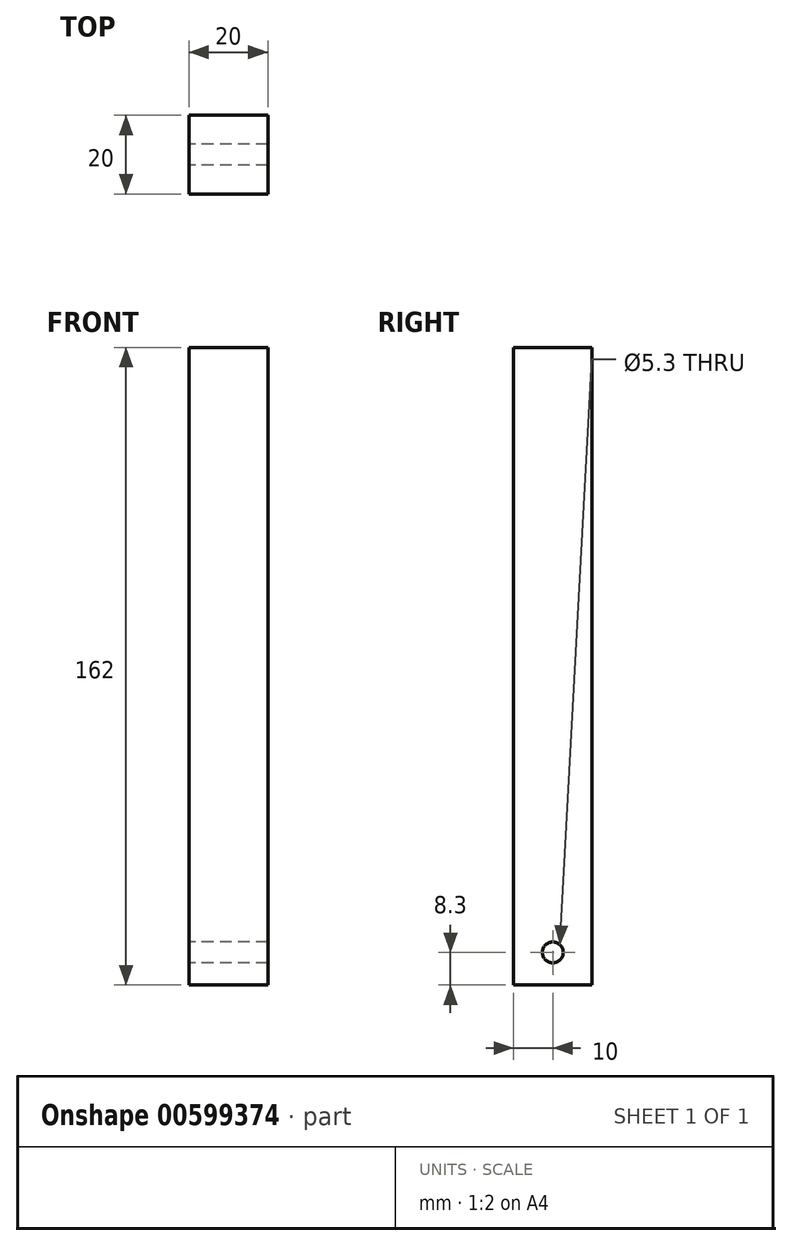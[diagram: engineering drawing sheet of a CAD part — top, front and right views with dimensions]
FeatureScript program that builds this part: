
annotation { "Feature Type Name" : "Feature", "Feature Type Description" : "" }
export const myFeature = defineFeature(function(context is Context, id is Id, definition is map)
    precondition{}
    {
        {
            var Q0;
            Q0=qCreatedBy(makeId("Top.planeOp"),FACE);
            var sketch = newSketch(context, id + "F0", { "sketchPlane" : qUnion([Q0])});
            skLineSegment(sketch, "E0.bottom", {"start": v(-10, 10) * mm, "end": v(10, 10) * mm});
            skLineSegment(sketch, "E0.top", {"start": v(-10, -10) * mm, "end": v(10, -10) * mm});
            skLineSegment(sketch, "E0.left", {"start": v(-10, 10) * mm, "end": v(-10, -10) * mm});
            skLineSegment(sketch, "E0.right", {"start": v(10, 10) * mm, "end": v(10, -10) * mm});
            skSolve(sketch);
        }
        {
            var Q0;
            Q0=qSketchRegion(id+"F0",true);
            extrude(context, id + "F1", {"entities" : qUnion([Q0]), "depth" : 162 * mm});
        }
        {
            var Q0;
            Q0=makeQuery(id+"F1.opExtrude","SWEPT_FACE",FACE,{"disambiguationData":[OSD([sQuery(id+"F0.wireOp",EDGE,"E0.right")])]});
            var sketch = newSketch(context, id + "F2", { "sketchPlane" : qUnion([Q0])});
            skCircle(sketch, "E1", {"center": v(0, 10) * mm, "radius": 2.5 * mm});
            skSolve(sketch);
        }
        {
            var Q0;
            Q0=makeQuery(id+"F1.opExtrude","SWEPT_FACE",FACE,{"disambiguationData":[OSD([sQuery(id+"F0.wireOp",EDGE,"E0.left")])]});
            var sketch = newSketch(context, id + "F3", { "sketchPlane" : qUnion([Q0])});
            skCircle(sketch, "E2", {"center": v(0, 8.3) * mm, "radius": 2.65 * mm});
            skPoint(sketch, "E2.centerSnap0", {"position": v(0, 162) * mm});
            skSolve(sketch);
        }
        {
            var Q0;
            Q0=qSketchRegion(id+"F3",true);
            extrude(context, id + "F4", {"entities" : qUnion([Q0]), "operationType" : NewBodyOperationType.REMOVE, "endBound" : BoundingType.THROUGH_ALL, "oppositeDirection" : true, "depth" : 25 * mm});
        }
    });
